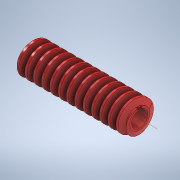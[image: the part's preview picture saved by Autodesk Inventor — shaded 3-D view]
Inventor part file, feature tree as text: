
AUTODESK INVENTOR PART (.ipt)
format: ipt  version: 2020.3 (Build 243373000, 373)  size: 494,080 bytes
history: native  units: mm (DEFAULTED — no unit token found)
features: other x6, extrude x2, chamfer x2, pattern_circular x2, sketch x2
ambient origin geometry x6: Origin, XZ Plane, X Axis, Y Axis, Z Axis, Center Point
bodies: Solid1 (feature_tree)
feature tree (14):
  extrude  "Base Body"  Depth=18.433962mm
  chamfer  "Chamfer1"  [1 undecoded]
  chamfer  "Chamfer2"  Distance=1.230059mm
  other  "Tooth Sketch"
  other  "Left Tooth"
  pattern_circular  "Left Tooth Pattern"  [2 undecoded]
  other  "Tooth"
  pattern_circular  "Tooth Pattern"  [2 undecoded]
  extrude  "Extrusion4"  Depth=10.0mm
  other  "Base Body Sketch"
  sketch  "Sketch5"  dims[d4=40.0mm d5=18.433962mm]
  other  "Srf1"
  sketch  "Sketch14"  dims[d6=63.5mm d7=0.0mm d8=1.230059mm d9=3.37956mm d10=1.230059mm d11=3.37956mm d12=19.198622mm d14=3.1425mm d24=19.198622mm d25=36.195mm d26=1.2065mm d27=5.837421mm d28=7.680818mm d29=9.309151mm d30=4.826mm d31=10.0mm d32=160.0mm d33=0.0mm d34=90.0deg d35=90.0deg d36=0.0mm d37=0.0mm d43=10.0mm d45=360.0deg d46=45.0deg d47=45.0deg d49=0.0mm d53=0.0mm d54=76.808176mm d55=0.0mm d56=0.0mm d57=15.361635mm d58=25.4mm d59=0.0mm d60=4.826mm d61=25.4mm d62=160.0mm d63=0.0mm d64=90.0deg d65=90.0deg d66=0.0mm d67=0.0mm d68=10.0mm d69=10.0mm d70=360.0deg d72=10.0mm d74=10.0mm d75=10.0mm d76=0.0mm d77=76.808176mm d123=0.15875mm d125=60.0deg d135=9.525mm d137=1.190625mm d138=1.230122mm d139=0.0mm]
  other  "Pitch Diameter"
note: 5 required parameter values undecoded (feature->parameter linkage not recoverable at this tier; creation-order binding heuristic only, values carry confidence <= 0.55)
